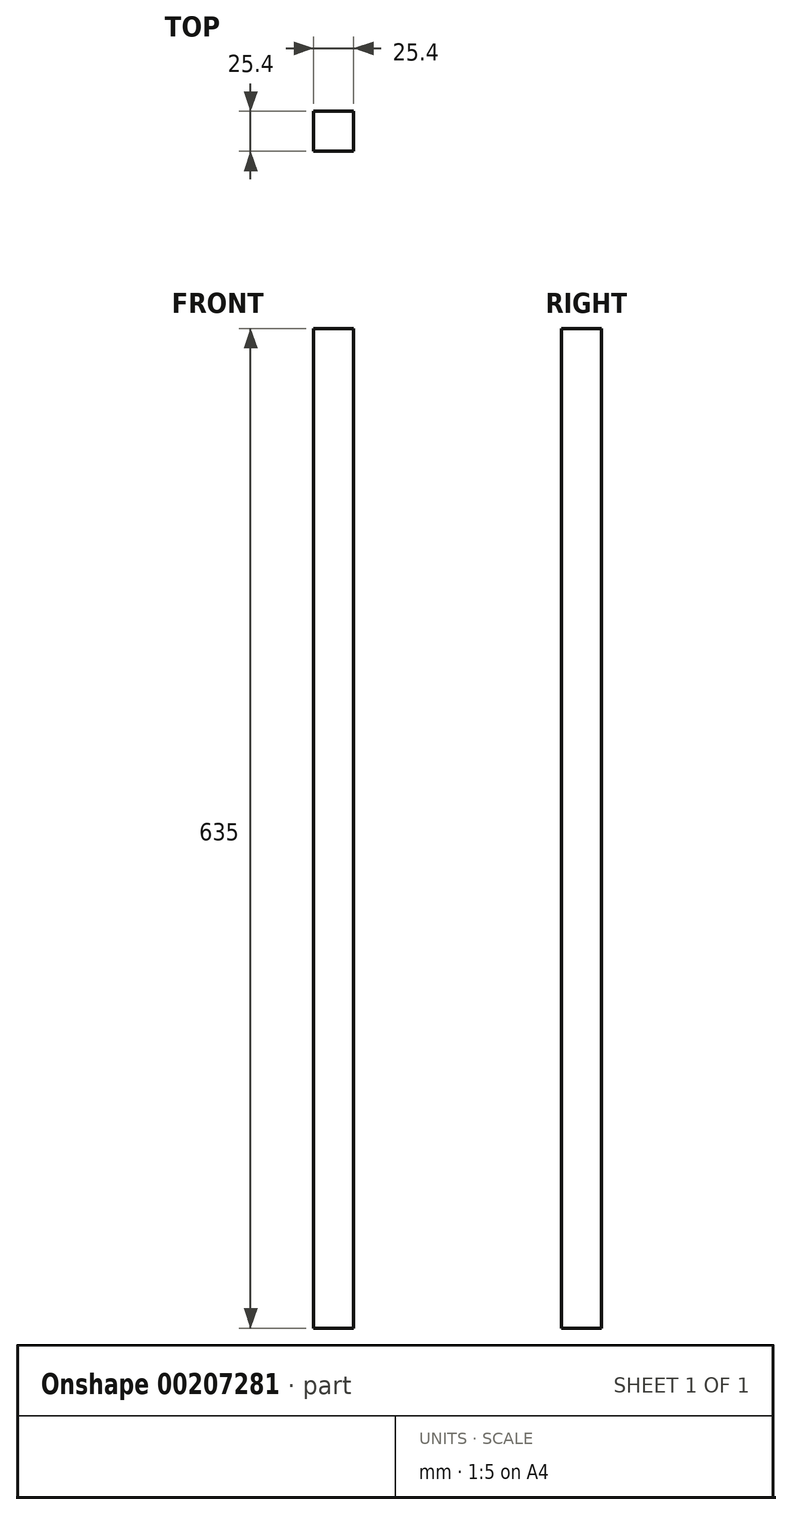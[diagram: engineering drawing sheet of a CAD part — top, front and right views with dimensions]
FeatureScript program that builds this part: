
annotation { "Feature Type Name" : "Feature", "Feature Type Description" : "" }
export const myFeature = defineFeature(function(context is Context, id is Id, definition is map)
    precondition{}
    {
        {
            var Q0;
            Q0=qCreatedBy(makeId("Front.planeOp"),FACE);
            var sketch = newSketch(context, id + "F0", { "sketchPlane" : qUnion([Q0])});
            skLineSegment(sketch, "E0.bottom", {"start": v(12.7, -317.5) * mm, "end": v(-12.7, -317.5) * mm});
            skLineSegment(sketch, "E0.top", {"start": v(12.7, 317.5) * mm, "end": v(-12.7, 317.5) * mm});
            skLineSegment(sketch, "E0.left", {"start": v(12.7, -317.5) * mm, "end": v(12.7, 317.5) * mm});
            skLineSegment(sketch, "E0.right", {"start": v(-12.7, -317.5) * mm, "end": v(-12.7, 317.5) * mm});
            skPoint(sketch, "E0.middle", {"position": v(0, 0) * mm});
            skSolve(sketch);
        }
        {
            var Q0;
            Q0 = qSketchRegion(id + "F0", true);
            extrude(context, id + "F1", {"entities" : qUnion([Q0]), "depth" : 25.4 * mm});
        }
    });
